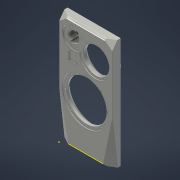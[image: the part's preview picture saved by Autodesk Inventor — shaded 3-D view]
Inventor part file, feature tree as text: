
AUTODESK INVENTOR PART (.ipt)
format: ipt  version: 2022 (Build 260153070, 153G)  size: 546,816 bytes
history: native  units: mm
features: other x24, sketch x15, chamfer x4, fillet x4, extrude x3, hole x3
ambient origin geometry x8: Origin, YZ Plane, XZ Plane, XY Plane, X Axis, Y Axis, Z Axis, Center Point
bodies: Body1 (feature_tree)
feature tree (53):
  other  "Аннотации"
  extrude  "Выдавливание2"  Depth=186.0mm
  hole  "Отверстие1"  [1 undecoded]
  extrude  "Выдавливание3"  Depth=102.0mm
  hole  "Отверстие3"  [1 undecoded]
  hole  "Отверстие4"  [1 undecoded]
  extrude  "Выдавливание4"  Depth=5.0mm
  sketch  "Эскиз9"
  sketch  "Эскиз10"
  other  "РабТочка1"
  other  "РабТочка2"
  other  "РабТочка3"
  other  "РабПлоскость1"
  other  "Разделение1"
  sketch  "Эскиз11"
  other  "РабТочка4"
  other  "РабТочка5"
  sketch  "Эскиз12"
  other  "РабТочка6"
  other  "РабПлоскость2"
  other  "Разделение2"
  sketch  "Эскиз13"
  sketch  "Эскиз14"
  sketch  "Эскиз15"
  other  "РабПлоскость3"
  other  "Разделение3"
  sketch  "Эскиз16"
  other  "РабПлоскость4"
  other  "Разделение4"
  chamfer  "Фаска1"  Distance=5.0mm
  chamfer  "Фаска2"  Distance=5.0mm
  chamfer  "Фаска3"  Distance=250.0mm
  chamfer  "Фаска4"  Distance=520.0mm
  fillet  "Сопряжение1"  Radius=120.0mm
  fillet  "Сопряжение2"  Radius=50.0mm
  fillet  "Сопряжение3"  Radius=40.0mm
  fillet  "Сопряжение4"  Radius=60.0mm
  sketch  "Эскиз17"
  sketch  "Эскиз1"
  sketch  "Эскиз3"
  sketch  "Эскиз4"
  sketch  "Эскиз6"
  sketch  "Эскиз7"
  sketch  "Эскиз8"
  other  "Линейный размер 1"
  other  "Линейный размер 2"
  other  "Линейный размер 3"
  other  "Линейный размер 4"
  other  "Линейный размер 5"
  other  "Линейный размер 6"
  other  "Линейный размер 7"
  other  "Линейный размер 8"
  other  "Линейный размер 9"
note: 3 required parameter values undecoded (feature->parameter linkage not recoverable at this tier; creation-order binding heuristic only, values carry confidence <= 0.55)
